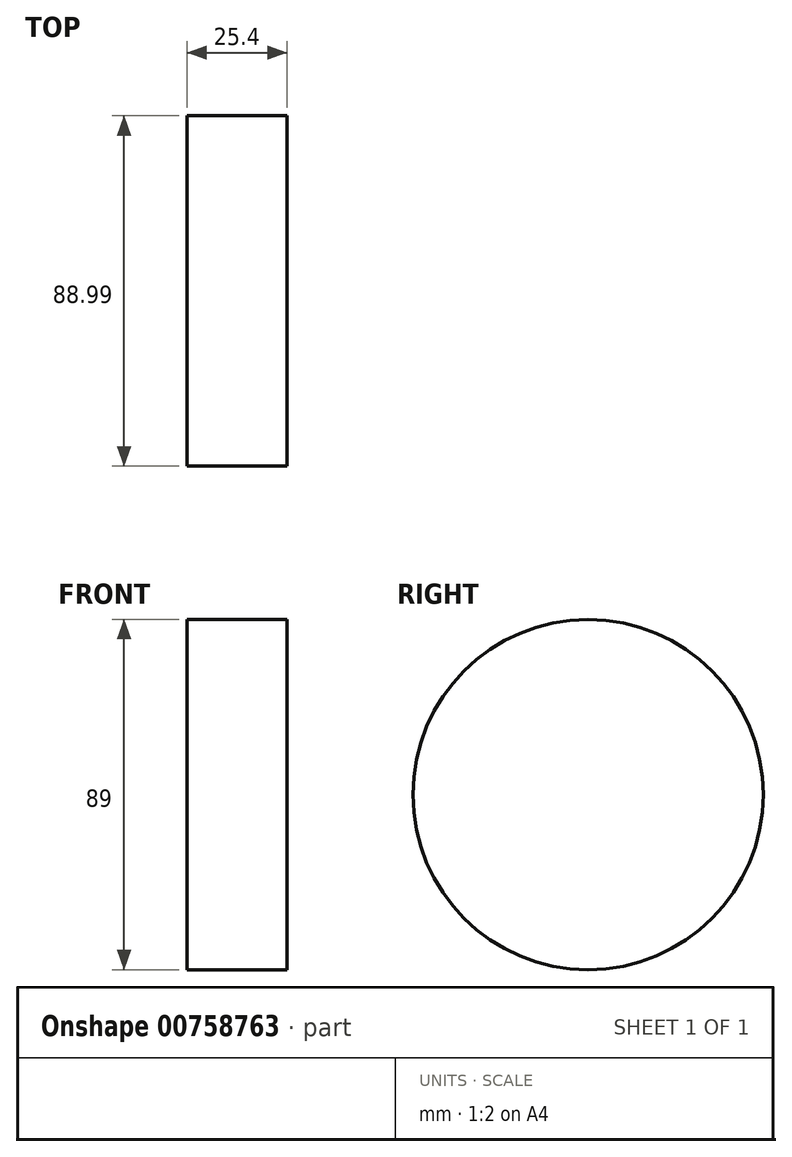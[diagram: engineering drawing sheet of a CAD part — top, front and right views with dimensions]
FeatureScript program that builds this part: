
annotation { "Feature Type Name" : "Feature", "Feature Type Description" : "" }
export const myFeature = defineFeature(function(context is Context, id is Id, definition is map)
    precondition{}
    {
        {
            var Q0;
            Q0=qCreatedBy(makeId("Right.planeOp"),FACE);
            var sketch = newSketch(context, id + "F0", { "sketchPlane" : qUnion([Q0])});
            skCircle(sketch, "E0", {"center": v(-53.75, 54.17) * mm, "radius": 44.5 * mm});
            skSolve(sketch);
        }
        {
            var Q0;
            Q0=makeQuery(id+"F0.imprint","IMPRINT",FACE,{"disambiguationData":[TD([[makeQuery(id+"F0.imprint","IMPRINT",EDGE,{"derivedFrom":sQuery(id+"F0.wireOp",EDGE,"E0")}),1.0]])]});
            extrude(context, id + "F1", {"entities" : qUnion([Q0]), "depth" : 25.4 * mm, "offsetDistance" : 25.4 * mm});
        }
    });
